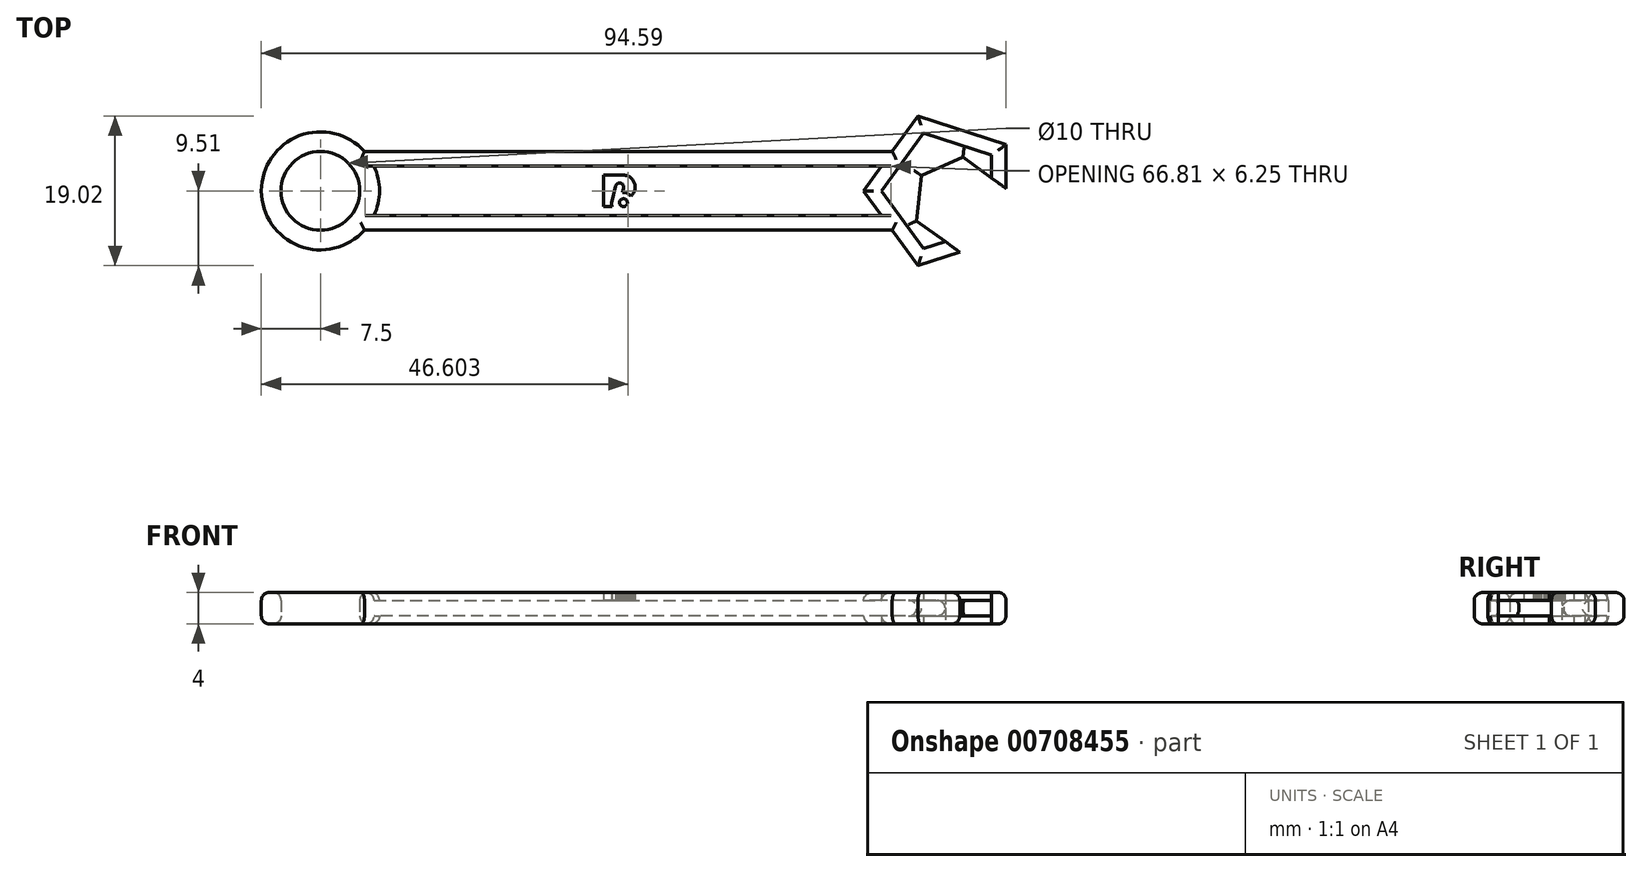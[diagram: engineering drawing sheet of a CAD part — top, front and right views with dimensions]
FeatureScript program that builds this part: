
annotation { "Feature Type Name" : "Feature", "Feature Type Description" : "" }
export const myFeature = defineFeature(function(context is Context, id is Id, definition is map)
    precondition{}
    {
        {
            var Q0;
            Q0=qCreatedBy(makeId("Top.planeOp"),FACE);
            var sketch = newSketch(context, id + "F0", { "sketchPlane" : qUnion([Q0])});
            skLineSegment(sketch, "E0.bottom", {"start": v(31.5, 5) * mm, "end": v(19.79, 5) * mm});
            skLineSegment(sketch, "E0.top", {"start": v(31.5, -5) * mm, "end": v(19.79, -5) * mm});
            skPoint(sketch, "E0.middle", {"position": v(0, 0) * mm});
            skCircle(sketch, "E1.cCircle", {"center": v(41.5, 0) * mm, "radius": 10 * mm, "construction": true});
            skLineSegment(sketch, "E1.0", {"start": v(31.5, 0) * mm, "end": v(38.4, 9.51) * mm});
            skLineSegment(sketch, "E1.1", {"start": v(38.4, 9.51) * mm, "end": v(49.6, 5.88) * mm});
            skLineSegment(sketch, "E1.2", {"start": v(49.6, 5.88) * mm, "end": v(49.6, 0.3) * mm});
            skLineSegment(sketch, "E1.3", {"start": v(43.71, -7.79) * mm, "end": v(38.4, -9.51) * mm});
            skLineSegment(sketch, "E1.4", {"start": v(38.4, -9.51) * mm, "end": v(31.5, 0) * mm});
            skLineSegment(sketch, "E2", {"start": v(31.5, 5) * mm, "end": v(35.13, 5) * mm});
            skLineSegment(sketch, "E3", {"start": v(31.5, -5) * mm, "end": v(35.13, -5) * mm});
            skCircle(sketch, "E4", {"center": v(-37.5, 0) * mm, "radius": 7.5 * mm});
            skPoint(sketch, "E5.orphan", {"position": v(-37.5, -5) * mm});
            skPoint(sketch, "E6.orphan", {"position": v(-37.5, 5) * mm});
            skCircle(sketch, "E7", {"center": v(-37.5, 0) * mm, "radius": 5 * mm});
            skLineSegment(sketch, "E8.bottom", {"start": v(-30, 3.12) * mm, "end": v(19.79, 3.12) * mm});
            skLineSegment(sketch, "E8.top", {"start": v(-30, -3.12) * mm, "end": v(19.79, -3.12) * mm});
            skLineSegment(sketch, "E9.bottom", {"start": v(24, 3.13) * mm, "end": v(31.5, 3.13) * mm});
            skLineSegment(sketch, "E9.top", {"start": v(24, -3.12) * mm, "end": v(31.5, -3.12) * mm});
            skLineSegment(sketch, "E10.bottom", {"start": v(-30, 3.12) * mm, "end": v(-30.68, 3.12) * mm});
            skLineSegment(sketch, "E10.top", {"start": v(-30, -3.12) * mm, "end": v(-30.68, -3.12) * mm});
            skLineSegment(sketch, "E11.bottom", {"start": v(31.5, 3.13) * mm, "end": v(33.77, 3.13) * mm});
            skLineSegment(sketch, "E11.top", {"start": v(31.5, -3.12) * mm, "end": v(33.77, -3.12) * mm});
            skLineSegment(sketch, "E12", {"start": v(46.46, 2.58) * mm, "end": v(49.6, 0.3) * mm});
            skLineSegment(sketch, "E13", {"start": v(40.58, -5.51) * mm, "end": v(43.71, -7.79) * mm});
            skPoint(sketch, "E14.orphan", {"position": v(49.6, -5.88) * mm});
            skPoint(sketch, "E15.start.orphan", {"position": v(45.55, -2.94) * mm});
            skLineSegment(sketch, "E16.0", {"start": v(42.92, -7.21) * mm, "end": v(38.25, -3.82) * mm});
            skLineSegment(sketch, "E16.1", {"start": v(38.25, -3.82) * mm, "end": v(38.85, 1.92) * mm});
            skLineSegment(sketch, "E16.2", {"start": v(38.85, 1.92) * mm, "end": v(44.13, 4.27) * mm});
            skLineSegment(sketch, "E16.3", {"start": v(44.13, 4.27) * mm, "end": v(48.8, 0.88) * mm});
            skPoint(sketch, "E16.0.midPoint", {"position": v(40.58, -5.51) * mm});
            skLineSegment(sketch, "E17.0", {"start": v(47.75, 4.54) * mm, "end": v(47.75, 1.64) * mm});
            skLineSegment(sketch, "E17.1", {"start": v(41.87, -6.45) * mm, "end": v(39.11, -7.35) * mm});
            skLineSegment(sketch, "E17.2", {"start": v(39.11, -7.35) * mm, "end": v(33.77, 0) * mm});
            skLineSegment(sketch, "E17.3", {"start": v(33.77, 0) * mm, "end": v(39.11, 7.35) * mm});
            skLineSegment(sketch, "E17.4", {"start": v(39.11, 7.35) * mm, "end": v(47.75, 4.54) * mm});
            skPoint(sketch, "E17.0.midPoint", {"position": v(47.75, 0) * mm});
            skPoint(sketch, "E18.orphan", {"position": v(47.75, -4.54) * mm});
            skLineSegment(sketch, "E19.trimOffspring", {"start": v(38.65, 0) * mm, "end": v(38.74, 0) * mm});
            skLineSegment(sketch, "E20.trimOffspring", {"start": v(19.79, -3.12) * mm, "end": v(24, -3.12) * mm});
            skLineSegment(sketch, "E21.trimOffspring", {"start": v(19.79, 3.13) * mm, "end": v(24, 3.13) * mm});
            skLineSegment(sketch, "E22.trimOffspring", {"start": v(19.79, -5) * mm, "end": v(-31.9, -5) * mm});
            skLineSegment(sketch, "E23.trimOffspring", {"start": v(19.79, 5) * mm, "end": v(-31.9, 5) * mm});
            skSolve(sketch);
        }
        {
            var Q0;
            {var subQ9=sQuery(id+"F0.wireOp",EDGE,"E1.1");Q0=makeQuery(id+"F0.imprint","IMPRINT",FACE,{"disambiguationData":[TD([[makeQuery(id+"F0.imprint","IMPRINT",EDGE,{"derivedFrom":subQ9}),-1.0]])]});}
            var Q1;
            {var subQ1=sQuery(id+"F0.wireOp",EDGE,"E0.top");Q1=makeQuery(id+"F0.imprint","IMPRINT",FACE,{"disambiguationData":[TD([[makeQuery(id+"F0.imprint","IMPRINT",EDGE,{"derivedFrom":subQ1}),-1.0]])]});}
            var Q2;
            {var subQ1=sQuery(id+"F0.wireOp",EDGE,"E0.bottom");Q2=makeQuery(id+"F0.imprint","IMPRINT",FACE,{"disambiguationData":[TD([[makeQuery(id+"F0.imprint","IMPRINT",EDGE,{"derivedFrom":subQ1}),1.0]])]});}
            var Q3;
            Q3=makeQuery(id+"F0.imprint","IMPRINT",FACE,{"disambiguationData":[TD([[makeQuery(id+"F0.imprint","IMPRINT",EDGE,{"derivedFrom":sQuery(id+"F0.wireOp",EDGE,"E7")}),-1.0]])]});
            extrude(context, id + "F1", {"entities" : qUnion([Q0, Q1, Q2, Q3]), "depth" : 2 * mm, "offsetDistance" : 25 * mm, "hasSecondDirection" : true, "secondDirectionOppositeDirection" : true, "secondDirectionDepth" : 2 * mm});
        }
        {
            var Q0;
            Q0=makeQuery(id+"F0.imprint","IMPRINT",FACE,{"disambiguationData":[TD([[makeQuery(id+"F0.imprint","IMPRINT",EDGE,{"derivedFrom":sQuery(id+"F0.wireOp",EDGE,"E8.bottom")}),-1.0]])]});
            var Q1;
            {var subQ0=sQuery(id+"F0.wireOp",EDGE,"E16.2");Q1=makeQuery(id+"F0.imprint","IMPRINT",FACE,{"disambiguationData":[TD([[makeQuery(id+"F0.imprint","IMPRINT",EDGE,{"derivedFrom":subQ0}),1.0]])]});}
            extrude(context, id + "F2", {"entities" : qUnion([Q0, Q1]), "operationType" : NewBodyOperationType.ADD, "depth" : 1 * mm, "offsetDistance" : 25 * mm, "hasSecondDirection" : true, "secondDirectionOppositeDirection" : true, "secondDirectionDepth" : 1 * mm});
        }
        {
            var Q0;
            {var subQ0=sQuery(id+"F0.wireOp",EDGE,"E4");Q0=makeQuery(id+"F1.opExtrude","CAP_EDGE",EDGE,{"disambiguationData":[OSD([subQ0]),TDD([makeQuery(id+"F0.imprint","IMPRINT",EDGE,{"disambiguationData":[TD([[makeQuery(id+"F0.imprint","INTERSECT",VERTEX,{"derivedFrom":[sQuery(id+"F0.wireOp",EDGE,"E0.bottom"),subQ0]}),-1.0]])],"derivedFrom":subQ0})])],"isStart":false});}
            var Q1;
            {var subQ0=sQuery(id+"F0.wireOp",EDGE,"E4");Q1=makeQuery(id+"F1.opExtrude","CAP_EDGE",EDGE,{"disambiguationData":[OSD([subQ0]),TDD([makeQuery(id+"F0.imprint","IMPRINT",EDGE,{"disambiguationData":[TD([[makeQuery(id+"F0.imprint","INTERSECT",VERTEX,{"derivedFrom":[sQuery(id+"F0.wireOp",EDGE,"E0.bottom"),subQ0]}),-1.0]])],"derivedFrom":subQ0})])],"isStart":true});}
            var Q2;
            Q2=makeQuery(id+"F1.opExtrude","CAP_EDGE",EDGE,{"disambiguationData":[OSD([sQuery(id+"F0.wireOp",EDGE,"E0.top"),sQuery(id+"F0.wireOp",EDGE,"E3")])],"isStart":false});
            var Q3;
            Q3=makeQuery(id+"F1.opExtrude","CAP_EDGE",EDGE,{"disambiguationData":[OSD([sQuery(id+"F0.wireOp",EDGE,"E0.top"),sQuery(id+"F0.wireOp",EDGE,"E3")])],"isStart":true});
            var Q4;
            Q4=makeQuery(id+"F1.opExtrude","CAP_EDGE",EDGE,{"disambiguationData":[OSD([sQuery(id+"F0.wireOp",EDGE,"E0.bottom"),sQuery(id+"F0.wireOp",EDGE,"E2")])],"isStart":false});
            var Q5;
            Q5=makeQuery(id+"F1.opExtrude","CAP_EDGE",EDGE,{"disambiguationData":[OSD([sQuery(id+"F0.wireOp",EDGE,"E0.bottom"),sQuery(id+"F0.wireOp",EDGE,"E2")])],"isStart":true});
            var Q6;
            Q6=makeQuery(id+"F1.opExtrude","CAP_EDGE",EDGE,{"disambiguationData":[OSD([sQuery(id+"F0.wireOp",EDGE,"E1.3")])],"isStart":true});
            var Q7;
            {var subQ0=sQuery(id+"F0.wireOp",EDGE,"E1.4");Q7=makeQuery(id+"F1.opExtrude","CAP_EDGE",EDGE,{"disambiguationData":[OSD([subQ0]),TDD([makeQuery(id+"F0.imprint","IMPRINT",EDGE,{"disambiguationData":[TD([[makeQuery(id+"F0.imprint","INTERSECT",VERTEX,{"derivedFrom":[sQuery(id+"F0.wireOp",EDGE,"E1.3"),subQ0]}),-1.0]])],"derivedFrom":subQ0})])],"isStart":true});}
            var Q8;
            Q8=makeQuery(id+"F1.opExtrude","CAP_EDGE",EDGE,{"disambiguationData":[OSD([sQuery(id+"F0.wireOp",EDGE,"E1.3")])],"isStart":false});
            var Q9;
            {var subQ0=sQuery(id+"F0.wireOp",EDGE,"E1.4");Q9=makeQuery(id+"F1.opExtrude","CAP_EDGE",EDGE,{"disambiguationData":[OSD([subQ0]),TDD([makeQuery(id+"F0.imprint","IMPRINT",EDGE,{"disambiguationData":[TD([[makeQuery(id+"F0.imprint","INTERSECT",VERTEX,{"derivedFrom":[sQuery(id+"F0.wireOp",EDGE,"E1.3"),subQ0]}),-1.0]])],"derivedFrom":subQ0})])],"isStart":false});}
            var Q10;
            {var subQ0=sQuery(id+"F0.wireOp",EDGE,"E1.0");Q10=makeQuery(id+"F1.opExtrude","CAP_EDGE",EDGE,{"disambiguationData":[OSD([subQ0]),TDD([makeQuery(id+"F0.imprint","IMPRINT",EDGE,{"disambiguationData":[TD([[makeQuery(id+"F0.imprint","INTERSECT",VERTEX,{"derivedFrom":[subQ0,sQuery(id+"F0.wireOp",EDGE,"E1.1")]}),1.0]])],"derivedFrom":subQ0})])],"isStart":false});}
            var Q11;
            Q11=makeQuery(id+"F1.opExtrude","CAP_EDGE",EDGE,{"disambiguationData":[OSD([sQuery(id+"F0.wireOp",EDGE,"E1.1")])],"isStart":false});
            var Q12;
            Q12=makeQuery(id+"F1.opExtrude","CAP_EDGE",EDGE,{"disambiguationData":[OSD([sQuery(id+"F0.wireOp",EDGE,"E1.2")])],"isStart":false});
            var Q13;
            {var subQ0=sQuery(id+"F0.wireOp",EDGE,"E1.0");Q13=makeQuery(id+"F1.opExtrude","CAP_EDGE",EDGE,{"disambiguationData":[OSD([subQ0]),TDD([makeQuery(id+"F0.imprint","IMPRINT",EDGE,{"disambiguationData":[TD([[makeQuery(id+"F0.imprint","INTERSECT",VERTEX,{"derivedFrom":[subQ0,sQuery(id+"F0.wireOp",EDGE,"E1.1")]}),1.0]])],"derivedFrom":subQ0})])],"isStart":true});}
            var Q14;
            Q14=makeQuery(id+"F1.opExtrude","CAP_EDGE",EDGE,{"disambiguationData":[OSD([sQuery(id+"F0.wireOp",EDGE,"E1.1")])],"isStart":true});
            var Q15;
            Q15=makeQuery(id+"F1.opExtrude","CAP_EDGE",EDGE,{"disambiguationData":[OSD([sQuery(id+"F0.wireOp",EDGE,"E1.2")])],"isStart":true});
            var Q16;
            Q16=makeQuery(id+"F1.opExtrude","CAP_EDGE",EDGE,{"disambiguationData":[OSD([sQuery(id+"F0.wireOp",EDGE,"E7")])],"isStart":false});
            var Q17;
            Q17=makeQuery(id+"F1.opExtrude","CAP_EDGE",EDGE,{"disambiguationData":[OSD([sQuery(id+"F0.wireOp",EDGE,"E7")])],"isStart":true});
            var Q18;
            {var subQ0=sQuery(id+"F0.wireOp",EDGE,"E1.0");Q18=makeQuery(id+"F1.opExtrude","CAP_EDGE",EDGE,{"disambiguationData":[OSD([subQ0]),TDD([makeQuery(id+"F0.imprint","IMPRINT",EDGE,{"disambiguationData":[TD([[makeQuery(id+"F0.imprint","INTERSECT",VERTEX,{"derivedFrom":[subQ0,sQuery(id+"F0.wireOp",EDGE,"E1.4")]}),-1.0]])],"derivedFrom":subQ0})])],"isStart":false});}
            var Q19;
            {var subQ0=sQuery(id+"F0.wireOp",EDGE,"E1.4");Q19=makeQuery(id+"F1.opExtrude","CAP_EDGE",EDGE,{"disambiguationData":[OSD([subQ0]),TDD([makeQuery(id+"F0.imprint","IMPRINT",EDGE,{"disambiguationData":[TD([[makeQuery(id+"F0.imprint","INTERSECT",VERTEX,{"derivedFrom":[sQuery(id+"F0.wireOp",EDGE,"E1.0"),subQ0]}),1.0]])],"derivedFrom":subQ0})])],"isStart":false});}
            var Q20;
            {var subQ0=sQuery(id+"F0.wireOp",EDGE,"E4");Q20=makeQuery(id+"F1.opExtrude","CAP_EDGE",EDGE,{"disambiguationData":[OSD([subQ0]),TDD([makeQuery(id+"F0.imprint","IMPRINT",EDGE,{"disambiguationData":[TD([[makeQuery(id+"F0.imprint","INTERSECT",VERTEX,{"derivedFrom":[subQ0,sQuery(id+"F0.wireOp",EDGE,"E10.bottom")]}),1.0]])],"derivedFrom":subQ0})])],"isStart":false});}
            var Q21;
            Q21=makeQuery(id+"F2.opExtrude","CAP_EDGE",EDGE,{"disambiguationData":[OSD([sQuery(id+"F0.wireOp",EDGE,"E16.3")])],"isStart":false});
            var Q22;
            Q22=makeQuery(id+"F2.opExtrude","CAP_EDGE",EDGE,{"disambiguationData":[OSD([sQuery(id+"F0.wireOp",EDGE,"E16.2")])],"isStart":false});
            var Q23;
            Q23=makeQuery(id+"F2.opExtrude","CAP_EDGE",EDGE,{"disambiguationData":[OSD([sQuery(id+"F0.wireOp",EDGE,"E16.1")])],"isStart":false});
            var Q24;
            Q24=makeQuery(id+"F2.opExtrude","CAP_EDGE",EDGE,{"disambiguationData":[OSD([sQuery(id+"F0.wireOp",EDGE,"E16.0")])],"isStart":false});
            var Q25;
            {var subQ0=sQuery(id+"F0.wireOp",EDGE,"E1.4");Q25=makeQuery(id+"F1.opExtrude","CAP_EDGE",EDGE,{"disambiguationData":[OSD([subQ0]),TDD([makeQuery(id+"F0.imprint","IMPRINT",EDGE,{"disambiguationData":[TD([[makeQuery(id+"F0.imprint","INTERSECT",VERTEX,{"derivedFrom":[sQuery(id+"F0.wireOp",EDGE,"E1.0"),subQ0]}),1.0]])],"derivedFrom":subQ0})])],"isStart":true});}
            var Q26;
            {var subQ0=sQuery(id+"F0.wireOp",EDGE,"E1.0");Q26=makeQuery(id+"F1.opExtrude","CAP_EDGE",EDGE,{"disambiguationData":[OSD([subQ0]),TDD([makeQuery(id+"F0.imprint","IMPRINT",EDGE,{"disambiguationData":[TD([[makeQuery(id+"F0.imprint","INTERSECT",VERTEX,{"derivedFrom":[subQ0,sQuery(id+"F0.wireOp",EDGE,"E1.4")]}),-1.0]])],"derivedFrom":subQ0})])],"isStart":true});}
            var Q27;
            {var subQ0=sQuery(id+"F0.wireOp",EDGE,"E4");Q27=makeQuery(id+"F1.opExtrude","CAP_EDGE",EDGE,{"disambiguationData":[OSD([subQ0]),TDD([makeQuery(id+"F0.imprint","IMPRINT",EDGE,{"disambiguationData":[TD([[makeQuery(id+"F0.imprint","INTERSECT",VERTEX,{"derivedFrom":[subQ0,sQuery(id+"F0.wireOp",EDGE,"E10.bottom")]}),1.0]])],"derivedFrom":subQ0})])],"isStart":true});}
            var Q28;
            Q28=makeQuery(id+"F2.opExtrude","CAP_EDGE",EDGE,{"disambiguationData":[OSD([sQuery(id+"F0.wireOp",EDGE,"E16.3")])],"isStart":true});
            var Q29;
            Q29=makeQuery(id+"F2.opExtrude","CAP_EDGE",EDGE,{"disambiguationData":[OSD([sQuery(id+"F0.wireOp",EDGE,"E16.2")])],"isStart":true});
            var Q30;
            Q30=makeQuery(id+"F2.opExtrude","CAP_EDGE",EDGE,{"disambiguationData":[OSD([sQuery(id+"F0.wireOp",EDGE,"E16.1")])],"isStart":true});
            var Q31;
            Q31=makeQuery(id+"F2.opExtrude","CAP_EDGE",EDGE,{"disambiguationData":[OSD([sQuery(id+"F0.wireOp",EDGE,"E16.0")])],"isStart":true});
            fillet(context, id + "F3", {"entities" : qUnion([Q0, Q1, Q2, Q3, Q4, Q5, Q6, Q7, Q8, Q9, Q10, Q11, Q12, Q13, Q14, Q15, Q16, Q17, Q18, Q19, Q20, Q21, Q22, Q23, Q24, Q25, Q26, Q27, Q28, Q29, Q30, Q31]), "radius" : 1 * mm, "tangentPropagation" : true, "allowEdgeOverflow" : false});
        }
        {
            var Q0;
            Q0=makeQuery(id+"F2.opExtrude","CAP_FACE",FACE,{"disambiguationData":[OSD([sQuery(id+"F0.wireOp",EDGE,"E1.0"),sQuery(id+"F0.wireOp",EDGE,"E1.4"),sQuery(id+"F0.wireOp",EDGE,"E4"),sQuery(id+"F0.wireOp",EDGE,"E8.bottom"),sQuery(id+"F0.wireOp",EDGE,"E8.top"),sQuery(id+"F0.wireOp",EDGE,"E9.bottom"),sQuery(id+"F0.wireOp",EDGE,"E9.top"),sQuery(id+"F0.wireOp",EDGE,"E10.bottom"),sQuery(id+"F0.wireOp",EDGE,"E10.top"),sQuery(id+"F0.wireOp",EDGE,"E11.bottom"),sQuery(id+"F0.wireOp",EDGE,"E11.top")])],"isStart":false});
            var sketch = newSketch(context, id + "F4", { "sketchPlane" : qUnion([Q0])});
            skLineSegment(sketch, "E24", {"start": v(1.05, -1) * mm, "end": v(1.02, -1) * mm});
            skLineSegment(sketch, "E25", {"start": v(1.02, -1) * mm, "end": v(0.95, -1) * mm});
            skLineSegment(sketch, "E26", {"start": v(0.95, -1) * mm, "end": v(0.85, -1.02) * mm});
            skLineSegment(sketch, "E27", {"start": v(0.85, -1.02) * mm, "end": v(0.76, -1.06) * mm});
            skLineSegment(sketch, "E28", {"start": v(0.76, -1.06) * mm, "end": v(0.68, -1.11) * mm});
            skLineSegment(sketch, "E29", {"start": v(0.68, -1.11) * mm, "end": v(0.6, -1.18) * mm});
            skLineSegment(sketch, "E30", {"start": v(0.6, -1.18) * mm, "end": v(0.55, -1.26) * mm});
            skLineSegment(sketch, "E31", {"start": v(0.55, -1.26) * mm, "end": v(0.51, -1.35) * mm});
            skLineSegment(sketch, "E32", {"start": v(0.51, -1.35) * mm, "end": v(0.5, -1.43) * mm});
            skLineSegment(sketch, "E33", {"start": v(0.5, -1.43) * mm, "end": v(0.5, -1.45) * mm});
            skLineSegment(sketch, "E34", {"start": v(0.5, -1.45) * mm, "end": v(0.5, -1.48) * mm});
            skLineSegment(sketch, "E35", {"start": v(0.5, -1.48) * mm, "end": v(0.5, -1.55) * mm});
            skLineSegment(sketch, "E36", {"start": v(0.5, -1.55) * mm, "end": v(0.51, -1.65) * mm});
            skLineSegment(sketch, "E37", {"start": v(0.51, -1.65) * mm, "end": v(0.55, -1.74) * mm});
            skLineSegment(sketch, "E38", {"start": v(0.55, -1.74) * mm, "end": v(0.6, -1.82) * mm});
            skLineSegment(sketch, "E39", {"start": v(0.6, -1.82) * mm, "end": v(0.67, -1.9) * mm});
            skLineSegment(sketch, "E40", {"start": v(0.67, -1.9) * mm, "end": v(0.75, -1.95) * mm});
            skLineSegment(sketch, "E41", {"start": v(0.75, -1.95) * mm, "end": v(0.84, -1.99) * mm});
            skLineSegment(sketch, "E42", {"start": v(0.84, -1.99) * mm, "end": v(0.91, -2) * mm});
            skLineSegment(sketch, "E43", {"start": v(0.91, -2) * mm, "end": v(0.94, -2) * mm});
            skLineSegment(sketch, "E44", {"start": v(0.94, -2) * mm, "end": v(0.96, -2) * mm});
            skLineSegment(sketch, "E45", {"start": v(0.96, -2) * mm, "end": v(1.04, -2) * mm});
            skLineSegment(sketch, "E46", {"start": v(1.04, -2) * mm, "end": v(1.14, -1.99) * mm});
            skLineSegment(sketch, "E47", {"start": v(1.14, -1.99) * mm, "end": v(1.23, -1.95) * mm});
            skLineSegment(sketch, "E48", {"start": v(1.23, -1.95) * mm, "end": v(1.3, -1.9) * mm});
            skLineSegment(sketch, "E49", {"start": v(1.3, -1.9) * mm, "end": v(1.38, -1.83) * mm});
            skLineSegment(sketch, "E50", {"start": v(1.38, -1.83) * mm, "end": v(1.43, -1.75) * mm});
            skLineSegment(sketch, "E51", {"start": v(1.43, -1.75) * mm, "end": v(1.47, -1.66) * mm});
            skLineSegment(sketch, "E52", {"start": v(1.47, -1.66) * mm, "end": v(1.5, -1.58) * mm});
            skLineSegment(sketch, "E53", {"start": v(1.5, -1.58) * mm, "end": v(1.5, -1.56) * mm});
            skLineSegment(sketch, "E54", {"start": v(1.5, -1.56) * mm, "end": v(1.5, -1.53) * mm});
            skLineSegment(sketch, "E55", {"start": v(1.5, -1.53) * mm, "end": v(1.5, -1.46) * mm});
            skLineSegment(sketch, "E56", {"start": v(1.5, -1.46) * mm, "end": v(1.48, -1.36) * mm});
            skLineSegment(sketch, "E57", {"start": v(1.48, -1.36) * mm, "end": v(1.44, -1.27) * mm});
            skLineSegment(sketch, "E58", {"start": v(1.44, -1.27) * mm, "end": v(1.39, -1.19) * mm});
            skLineSegment(sketch, "E59", {"start": v(1.39, -1.19) * mm, "end": v(1.32, -1.12) * mm});
            skLineSegment(sketch, "E60", {"start": v(1.32, -1.12) * mm, "end": v(1.24, -1.06) * mm});
            skLineSegment(sketch, "E61", {"start": v(1.24, -1.06) * mm, "end": v(1.15, -1.03) * mm});
            skLineSegment(sketch, "E62", {"start": v(1.15, -1.03) * mm, "end": v(1.07, -1) * mm});
            skLineSegment(sketch, "E63", {"start": v(1.07, -1) * mm, "end": v(1.05, -1) * mm});
            skLineSegment(sketch, "E64", {"start": v(0.98, 1.99) * mm, "end": v(1.02, 1.99) * mm});
            skLineSegment(sketch, "E65", {"start": v(1.02, 1.99) * mm, "end": v(1.13, 1.98) * mm});
            skLineSegment(sketch, "E66", {"start": v(1.13, 1.98) * mm, "end": v(1.28, 1.96) * mm});
            skLineSegment(sketch, "E67", {"start": v(1.28, 1.96) * mm, "end": v(1.42, 1.92) * mm});
            skLineSegment(sketch, "E68", {"start": v(1.42, 1.92) * mm, "end": v(1.56, 1.87) * mm});
            skLineSegment(sketch, "E69", {"start": v(1.56, 1.87) * mm, "end": v(1.7, 1.8) * mm});
            skLineSegment(sketch, "E70", {"start": v(1.7, 1.8) * mm, "end": v(1.82, 1.73) * mm});
            skLineSegment(sketch, "E71", {"start": v(1.82, 1.73) * mm, "end": v(1.93, 1.64) * mm});
            skLineSegment(sketch, "E72", {"start": v(1.93, 1.64) * mm, "end": v(2.04, 1.55) * mm});
            skLineSegment(sketch, "E73", {"start": v(2.04, 1.55) * mm, "end": v(2.14, 1.44) * mm});
            skLineSegment(sketch, "E74", {"start": v(2.14, 1.44) * mm, "end": v(2.22, 1.33) * mm});
            skLineSegment(sketch, "E75", {"start": v(2.22, 1.33) * mm, "end": v(2.3, 1.2) * mm});
            skLineSegment(sketch, "E76", {"start": v(2.3, 1.2) * mm, "end": v(2.36, 1.07) * mm});
            skLineSegment(sketch, "E77", {"start": v(2.36, 1.07) * mm, "end": v(2.41, 0.93) * mm});
            skLineSegment(sketch, "E78", {"start": v(2.41, 0.93) * mm, "end": v(2.45, 0.8) * mm});
            skLineSegment(sketch, "E79", {"start": v(2.45, 0.8) * mm, "end": v(2.47, 0.64) * mm});
            skLineSegment(sketch, "E80", {"start": v(2.47, 0.64) * mm, "end": v(2.48, 0.53) * mm});
            skLineSegment(sketch, "E81", {"start": v(2.48, 0.53) * mm, "end": v(2.48, 0.5) * mm});
            skLineSegment(sketch, "E82", {"start": v(2.48, 0.5) * mm, "end": v(2.48, 0.45) * mm});
            skLineSegment(sketch, "E83", {"start": v(2.48, 0.45) * mm, "end": v(2.47, 0.32) * mm});
            skLineSegment(sketch, "E84", {"start": v(2.47, 0.32) * mm, "end": v(2.44, 0.16) * mm});
            skLineSegment(sketch, "E85", {"start": v(2.44, 0.16) * mm, "end": v(2.4, 0) * mm});
            skLineSegment(sketch, "E86", {"start": v(2.4, 0) * mm, "end": v(2.34, -0.15) * mm});
            skLineSegment(sketch, "E87", {"start": v(2.34, -0.15) * mm, "end": v(2.26, -0.3) * mm});
            skLineSegment(sketch, "E88", {"start": v(2.26, -0.3) * mm, "end": v(2.17, -0.42) * mm});
            skLineSegment(sketch, "E89", {"start": v(2.17, -0.42) * mm, "end": v(2.06, -0.54) * mm});
            skLineSegment(sketch, "E90", {"start": v(2.06, -0.54) * mm, "end": v(1.98, -0.63) * mm});
            skLineSegment(sketch, "E91", {"start": v(1.98, -0.63) * mm, "end": v(1.95, -0.65) * mm});
            skLineSegment(sketch, "E92", {"start": v(1.95, -0.65) * mm, "end": v(1.91, -0.61) * mm});
            skLineSegment(sketch, "E93", {"start": v(1.91, -0.61) * mm, "end": v(1.8, -0.51) * mm});
            skLineSegment(sketch, "E94", {"start": v(1.8, -0.51) * mm, "end": v(1.63, -0.4) * mm});
            skLineSegment(sketch, "E95", {"start": v(1.63, -0.4) * mm, "end": v(1.45, -0.3) * mm});
            skLineSegment(sketch, "E96", {"start": v(1.45, -0.3) * mm, "end": v(1.3, -0.24) * mm});
            skLineSegment(sketch, "E97", {"start": v(1.3, -0.24) * mm, "end": v(1.24, -0.23) * mm});
            skLineSegment(sketch, "E98", {"start": v(1.24, -0.23) * mm, "end": v(1.21, -0.22) * mm});
            skLineSegment(sketch, "E99", {"start": v(1.21, -0.22) * mm, "end": v(1.05, -0.2) * mm});
            skLineSegment(sketch, "E100", {"start": v(1.05, -0.2) * mm, "end": v(0.88, -0.19) * mm});
            skLineSegment(sketch, "E101", {"start": v(0.88, -0.19) * mm, "end": v(0.85, -0.19) * mm});
            skLineSegment(sketch, "E102", {"start": v(0.85, -0.19) * mm, "end": v(1, 0.37) * mm});
            skLineSegment(sketch, "E103", {"start": v(1, 0.37) * mm, "end": v(1, 0.4) * mm});
            skLineSegment(sketch, "E104", {"start": v(1, 0.4) * mm, "end": v(1, 0.48) * mm});
            skLineSegment(sketch, "E105", {"start": v(1, 0.48) * mm, "end": v(1, 0.58) * mm});
            skLineSegment(sketch, "E106", {"start": v(1, 0.58) * mm, "end": v(0.98, 0.67) * mm});
            skLineSegment(sketch, "E107", {"start": v(0.98, 0.67) * mm, "end": v(0.94, 0.76) * mm});
            skLineSegment(sketch, "E108", {"start": v(0.94, 0.76) * mm, "end": v(0.88, 0.84) * mm});
            skLineSegment(sketch, "E109", {"start": v(0.88, 0.84) * mm, "end": v(0.8, 0.9) * mm});
            skLineSegment(sketch, "E110", {"start": v(0.8, 0.9) * mm, "end": v(0.72, 0.96) * mm});
            skLineSegment(sketch, "E111", {"start": v(0.72, 0.96) * mm, "end": v(0.65, 0.99) * mm});
            skLineSegment(sketch, "E112", {"start": v(0.65, 0.99) * mm, "end": v(0.62, 1) * mm});
            skLineSegment(sketch, "E113", {"start": v(0.62, 1) * mm, "end": v(0.6, 1) * mm});
            skLineSegment(sketch, "E114", {"start": v(0.6, 1) * mm, "end": v(0.52, 1) * mm});
            skLineSegment(sketch, "E115", {"start": v(0.52, 1) * mm, "end": v(0.42, 1) * mm});
            skLineSegment(sketch, "E116", {"start": v(0.42, 1) * mm, "end": v(0.33, 0.98) * mm});
            skLineSegment(sketch, "E117", {"start": v(0.33, 0.98) * mm, "end": v(0.24, 0.93) * mm});
            skLineSegment(sketch, "E118", {"start": v(0.24, 0.93) * mm, "end": v(0.16, 0.88) * mm});
            skLineSegment(sketch, "E119", {"start": v(0.16, 0.88) * mm, "end": v(0.1, 0.8) * mm});
            skLineSegment(sketch, "E120", {"start": v(0.1, 0.8) * mm, "end": v(0.04, 0.72) * mm});
            skLineSegment(sketch, "E121", {"start": v(0.04, 0.72) * mm, "end": v(0.01, 0.65) * mm});
            skLineSegment(sketch, "E122", {"start": v(0.01, 0.65) * mm, "end": v(0, 0.62) * mm});
            skLineSegment(sketch, "E123", {"start": v(0, 0.62) * mm, "end": v(-0.47, -1.26) * mm});
            skLineSegment(sketch, "E124", {"start": v(-0.47, -1.26) * mm, "end": v(-0.47, -1.26) * mm});
            skLineSegment(sketch, "E125", {"start": v(-0.47, -1.26) * mm, "end": v(-0.48, -1.31) * mm});
            skLineSegment(sketch, "E126", {"start": v(-0.48, -1.31) * mm, "end": v(-0.5, -1.45) * mm});
            skLineSegment(sketch, "E127", {"start": v(-0.5, -1.45) * mm, "end": v(-0.5, -1.64) * mm});
            skLineSegment(sketch, "E128", {"start": v(-0.5, -1.64) * mm, "end": v(-0.49, -1.82) * mm});
            skLineSegment(sketch, "E129", {"start": v(-0.49, -1.82) * mm, "end": v(-0.46, -1.96) * mm});
            skLineSegment(sketch, "E130", {"start": v(-0.46, -1.96) * mm, "end": v(-0.45, -2) * mm});
            skLineSegment(sketch, "E131", {"start": v(-0.45, -2) * mm, "end": v(-1.5, -2) * mm});
            skLineSegment(sketch, "E132", {"start": v(-1.5, -2) * mm, "end": v(-1.5, 2) * mm});
            skLineSegment(sketch, "E133", {"start": v(-1.5, 1.99) * mm, "end": v(0.98, 1.99) * mm});
            skSolve(sketch);
        }
        {
            var Q0;
            Q0 = qSketchRegion(id + "F4", true);
            extrude(context, id + "F5", {"entities" : qUnion([Q0]), "operationType" : NewBodyOperationType.ADD, "depth" : 1 * mm, "offsetDistance" : 25 * mm});
        }
    });
